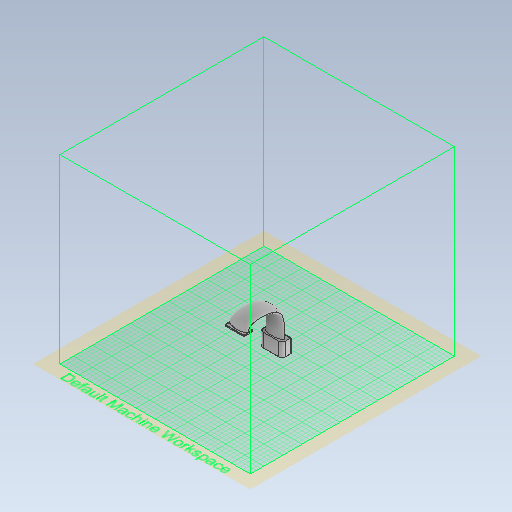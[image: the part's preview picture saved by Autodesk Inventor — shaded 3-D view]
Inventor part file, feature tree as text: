
AUTODESK INVENTOR PART (.ipt)
format: ipt  version: 2021 (Build 250183000, 183)  size: 633,344 bytes
history: native  units: mm
features: sketch x4, extrude x2, plane x1
ambient origin geometry x8: Origin, YZ Plane, XZ Plane, XY Plane, X Axis, Y Axis, Z Axis, Center Point
bodies: Volumenkörper1 (feature_tree)
feature tree (7):
  sketch  "Skizze1"  dims[d0=50.0mm d1=30.0mm]
  extrude  "Extrusion1"  Depth=30.0mm
  plane  "Arbeitsebene1"
  extrude  "Extrusion7"  Depth=53.0mm
  sketch  "Skizze11"  dims[d44=50.0mm]
  sketch  "Skizze12"  dims[d45=35.0mm d46=55.0mm d47=3.0mm d48=0.0mm d49=10.0mm d50=25.0mm d51=20.0mm d52=7.5mm d54=10.0mm d59=4.090145mm d60=5.997518mm d61=10.884207mm d62=3.644932mm d63=12.063032mm d64=16.810244mm d65=34.889086mm d66=17.5mm d67=60.11846mm d68=90.0mm d69=9.683046mm d70=9.999917mm d71=15.667339mm]
  sketch  "Skizze10"  dims[d2=20.0mm d3=0.0mm d7=53.0mm]
